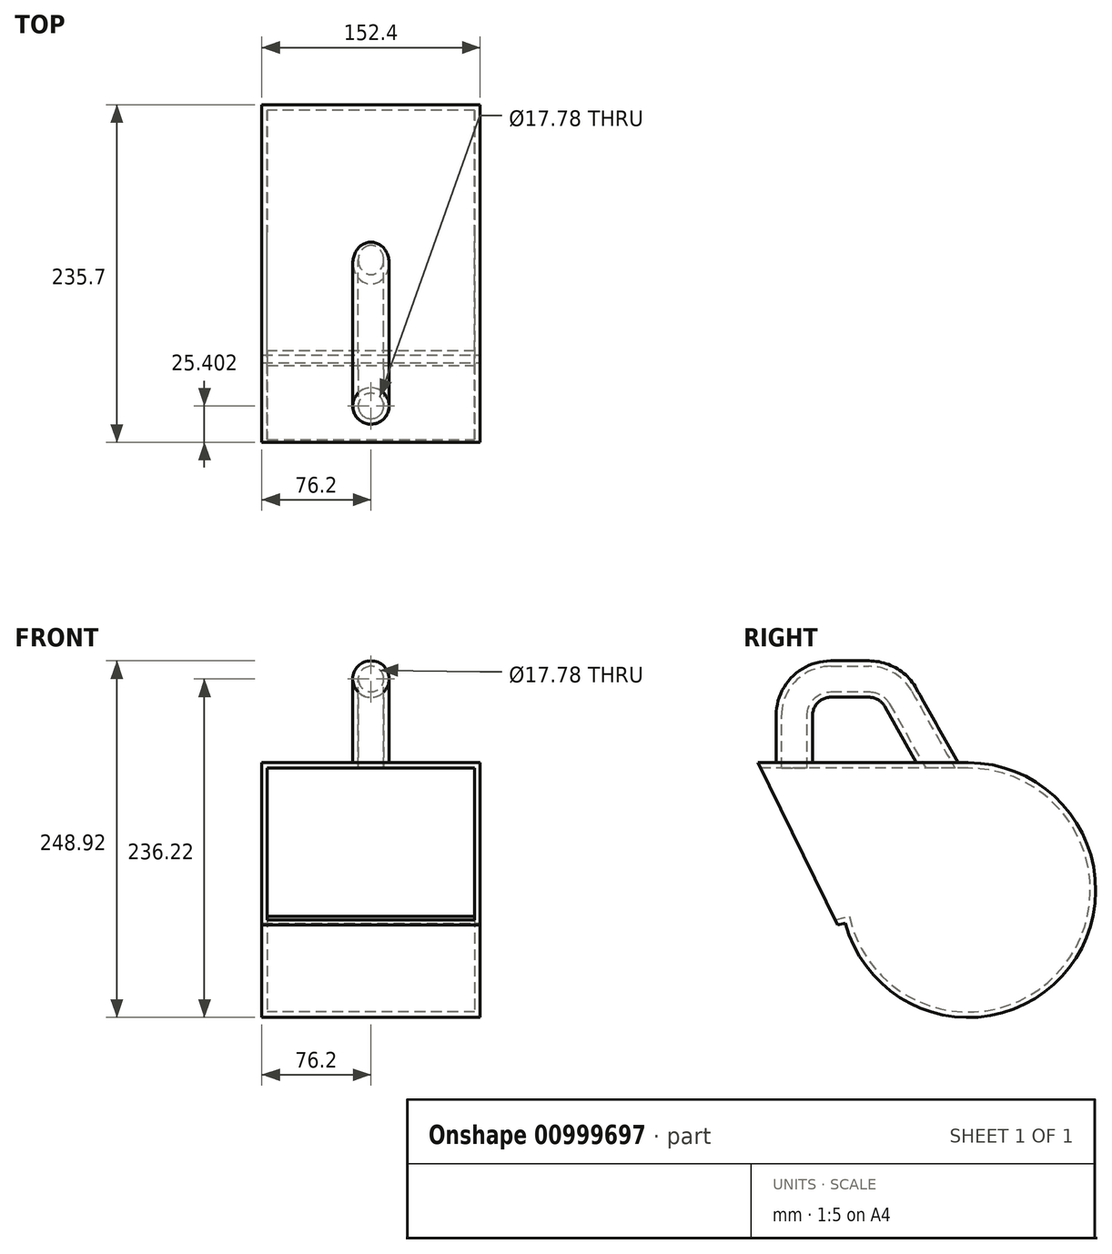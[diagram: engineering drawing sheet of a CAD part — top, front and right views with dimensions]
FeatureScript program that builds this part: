
annotation { "Feature Type Name" : "Feature", "Feature Type Description" : "" }
export const myFeature = defineFeature(function(context is Context, id is Id, definition is map)
    precondition{}
    {
        {
            var Q0;
            Q0=qCreatedBy(makeId("Right.planeOp"),FACE);
            var sketch = newSketch(context, id + "F0", { "sketchPlane" : qUnion([Q0])});
            skCircle(sketch, "E0", {"center": v(0, 0) * mm, "radius": 88.9 * mm});
            skSolve(sketch);
        }
        {
            var Q0;
            Q0 = qSketchRegion(id + "F0", true);
            extrude(context, id + "F1", {"entities" : qUnion([Q0]), "depth" : 152.4 * mm, "offsetDistance" : 25.4 * mm});
        }
        {
            var Q0;
            Q0=makeQuery(id+"F1.opExtrude","CAP_FACE",FACE,{"disambiguationData":[OSD([sQuery(id+"F0.wireOp",EDGE,"E0")])],"isStart":false});
            var sketch = newSketch(context, id + "F2", { "sketchPlane" : qUnion([Q0])});
            skLineSegment(sketch, "E1", {"start": v(91.94, 34.69) * mm, "end": v(91.94, -204.72) * mm});
            skLineSegment(sketch, "E2", {"start": v(0, 88.9) * mm, "end": v(-146.8, 88.9) * mm});
            skLineSegment(sketch, "E3", {"start": v(-146.8, 88.9) * mm, "end": v(-91.3, -24.46) * mm});
            skLineSegment(sketch, "E4", {"start": v(-91.3, -24.46) * mm, "end": v(0, 0) * mm});
            skLineSegment(sketch, "E5", {"start": v(0, 0) * mm, "end": v(0, 88.9) * mm});
            skSolve(sketch);
        }
        {
            var Q0;
            {var subQ0=sQuery(id+"F2.wireOp",EDGE,"E2");Q0=makeQuery(id+"F2.imprint","IMPRINT",FACE,{"disambiguationData":[TD([[makeQuery(id+"F2.imprint","IMPRINT",EDGE,{"derivedFrom":subQ0}),1.0]])]});}
            var Q1;
            Q1=makeQuery(id+"F1.opExtrude","CAP_FACE",FACE,{"disambiguationData":[OSD([sQuery(id+"F0.wireOp",EDGE,"E0")])],"isStart":true});
            extrude(context, id + "F3", {"entities" : qUnion([Q0]), "operationType" : NewBodyOperationType.ADD, "endBound" : BoundingType.UP_TO_SURFACE, "oppositeDirection" : true, "depth" : 25.4 * mm, "endBoundEntityFace" : qUnion([Q1]), "offsetDistance" : 25.4 * mm});
        }
        {
            var Q0;
            {var subQ0=sQuery(id+"F0.wireOp",EDGE,"E0");Q0=makeQuery(id+"F3.boolean.opBoolean","MERGE",FACE,{"derivedFrom":[makeQuery(id+"F1.opExtrude","CAP_FACE",FACE,{"disambiguationData":[OSD([subQ0])],"isStart":false}),makeQuery(id+"F3.opExtrude","CAP_FACE",FACE,{"disambiguationData":[OSD([subQ0,sQuery(id+"F2.wireOp",EDGE,"E2"),sQuery(id+"F2.wireOp",EDGE,"E3"),sQuery(id+"F2.wireOp",EDGE,"E4")])],"isStart":true})]});}
            var Q1;
            {var subQ0=sQuery(id+"F0.wireOp",EDGE,"E0");Q1=makeQuery(id+"F3.boolean.opBoolean","MERGE",FACE,{"derivedFrom":[makeQuery(id+"F1.opExtrude","CAP_FACE",FACE,{"disambiguationData":[OSD([subQ0])],"isStart":true}),makeQuery(id+"F3.opExtrude","CAP_FACE",FACE,{"disambiguationData":[OSD([subQ0,sQuery(id+"F2.wireOp",EDGE,"E2"),sQuery(id+"F2.wireOp",EDGE,"E3"),sQuery(id+"F2.wireOp",EDGE,"E4")])],"isStart":false})]});}
            cPlane(context, id + "F4", {"entities" : qUnion([Q0, Q1]), "cplaneType" : CPlaneType.MID_PLANE, "offset" : 25.4 * mm, "width" : 152.4 * mm, "height" : 152.4 * mm});
        }
        {
            var Q0;
            Q0=qCreatedBy(id+"F4.planeOp",FACE);
            var sketch = newSketch(context, id + "F5", { "sketchPlane" : qUnion([Q0])});
            skLineSegment(sketch, "E6", {"start": v(-108.7, 88.9) * mm, "end": v(-108.7, 134.62) * mm});
            skLineSegment(sketch, "E7", {"start": v(-108.7, 134.62) * mm, "end": v(-61.93, 134.62) * mm});
            skLineSegment(sketch, "E8", {"start": v(-61.93, 134.62) * mm, "end": v(-36.23, 88.9) * mm});
            skLineSegment(sketch, "E9.0", {"start": v(-47.07, 160.02) * mm, "end": v(-7.1, 88.9) * mm});
            skLineSegment(sketch, "E9.1", {"start": v(-134.1, 160.02) * mm, "end": v(-47.07, 160.02) * mm});
            skLineSegment(sketch, "E9.2", {"start": v(-134.1, 88.9) * mm, "end": v(-134.1, 160.02) * mm});
            skLineSegment(sketch, "E10", {"start": v(-134.1, 88.9) * mm, "end": v(-108.7, 88.9) * mm});
            skLineSegment(sketch, "E11", {"start": v(-36.23, 88.9) * mm, "end": v(-7.1, 88.9) * mm});
            skSolve(sketch);
        }
        {
            var Q0;
            Q0=makeQuery(id+"F5.imprint","IMPRINT",FACE,{"disambiguationData":[TD([[makeQuery(id+"F5.imprint","IMPRINT",EDGE,{"derivedFrom":sQuery(id+"F5.wireOp",EDGE,"E6")}),1.0]])]});
            extrude(context, id + "F6", {"entities" : qUnion([Q0]), "operationType" : NewBodyOperationType.ADD, "depth" : 12.7 * mm, "offsetDistance" : 25.4 * mm, "hasSecondDirection" : true, "secondDirectionOppositeDirection" : true, "secondDirectionDepth" : 12.7 * mm});
        }
        {
            var Q0;
            Q0=makeQuery(id+"F6.opExtrude","SWEPT_EDGE",EDGE,{"disambiguationData":[OSD([sQuery(id+"F5.wireOp",EDGE,"E6"),sQuery(id+"F5.wireOp",EDGE,"E7")])]});
            var Q1;
            Q1=makeQuery(id+"F6.opExtrude","SWEPT_EDGE",EDGE,{"disambiguationData":[OSD([sQuery(id+"F5.wireOp",EDGE,"E7"),sQuery(id+"F5.wireOp",EDGE,"E8")])]});
            fillet(context, id + "F7", {"entities" : qUnion([Q0, Q1]), "radius" : 12.7 * mm, "tangentPropagation" : true, "allowEdgeOverflow" : false});
        }
        {
            var Q0;
            Q0=makeQuery(id+"F6.opExtrude","CAP_FACE",FACE,{"disambiguationData":[OSD([sQuery(id+"F5.wireOp",EDGE,"E6"),sQuery(id+"F5.wireOp",EDGE,"E7"),sQuery(id+"F5.wireOp",EDGE,"E8"),sQuery(id+"F5.wireOp",EDGE,"E9.0"),sQuery(id+"F5.wireOp",EDGE,"E9.1"),sQuery(id+"F5.wireOp",EDGE,"E9.2"),sQuery(id+"F5.wireOp",EDGE,"E10"),sQuery(id+"F5.wireOp",EDGE,"E11")])],"isStart":false});
            var sketch = newSketch(context, id + "F8", { "sketchPlane" : qUnion([Q0])});
            skLineSegment(sketch, "E12", {"start": v(-134.1, 160.02) * mm, "end": v(-134.1, 121.92) * mm});
            skArc(sketch, "E13", {"start": v(-96, 160.02) * mm, "mid": v(-122.94, 148.86) * mm, "end": v(-134.1, 121.92) * mm});
            skLineSegment(sketch, "E14", {"start": v(-134.1, 160.02) * mm, "end": v(-96, 160.02) * mm});
            skLineSegment(sketch, "E15", {"start": v(-47.07, 160.02) * mm, "end": v(-69.36, 160.02) * mm});
            skArc(sketch, "E16", {"start": v(-36.14, 140.59) * mm, "mid": v(-50.12, 154.8) * mm, "end": v(-69.36, 160.02) * mm});
            skLineSegment(sketch, "E17", {"start": v(-47.07, 160.02) * mm, "end": v(-36.14, 140.59) * mm});
            skSolve(sketch);
        }
        {
            var Q0;
            Q0=makeQuery(id+"F8.imprint","IMPRINT",FACE,{"disambiguationData":[TD([[makeQuery(id+"F8.imprint","IMPRINT",EDGE,{"derivedFrom":sQuery(id+"F8.wireOp",EDGE,"E12")}),-1.0]])]});
            var Q1;
            Q1=makeQuery(id+"F8.imprint","IMPRINT",FACE,{"disambiguationData":[TD([[makeQuery(id+"F8.imprint","IMPRINT",EDGE,{"derivedFrom":sQuery(id+"F8.wireOp",EDGE,"E15")}),-1.0]])]});
            extrude(context, id + "F9", {"entities" : qUnion([Q0, Q1]), "operationType" : NewBodyOperationType.REMOVE, "endBound" : BoundingType.UP_TO_NEXT, "oppositeDirection" : true, "depth" : 25.4 * mm, "offsetDistance" : 25.4 * mm});
        }
        {
            var Q0;
            Q0=makeQuery(id+"F6.opExtrude","CAP_EDGE",EDGE,{"disambiguationData":[OSD([sQuery(id+"F5.wireOp",EDGE,"E9.2")])],"isStart":false});
            var Q1;
            Q1=makeQuery(id+"F6.opExtrude","CAP_EDGE",EDGE,{"disambiguationData":[OSD([sQuery(id+"F5.wireOp",EDGE,"E6")])],"isStart":false});
            var Q2;
            Q2=makeQuery(id+"F6.opExtrude","CAP_EDGE",EDGE,{"disambiguationData":[OSD([sQuery(id+"F5.wireOp",EDGE,"E9.2")])],"isStart":true});
            var Q3;
            Q3=makeQuery(id+"F6.opExtrude","CAP_EDGE",EDGE,{"disambiguationData":[OSD([sQuery(id+"F5.wireOp",EDGE,"E6")])],"isStart":true});
            fillet(context, id + "F10", {"entities" : qUnion([Q0, Q1, Q2, Q3]), "radius" : 12.7 * mm, "tangentPropagation" : true, "allowEdgeOverflow" : false});
        }
        {
            var Q0;
            Q0=makeQuery(id+"F3.opExtrude","SWEPT_FACE",FACE,{"disambiguationData":[OSD([sQuery(id+"F2.wireOp",EDGE,"E3")])]});
            shell(context, id + "F11", {"entities" : qUnion([Q0]), "thickness" : 3.8 * mm});
        }
    });
